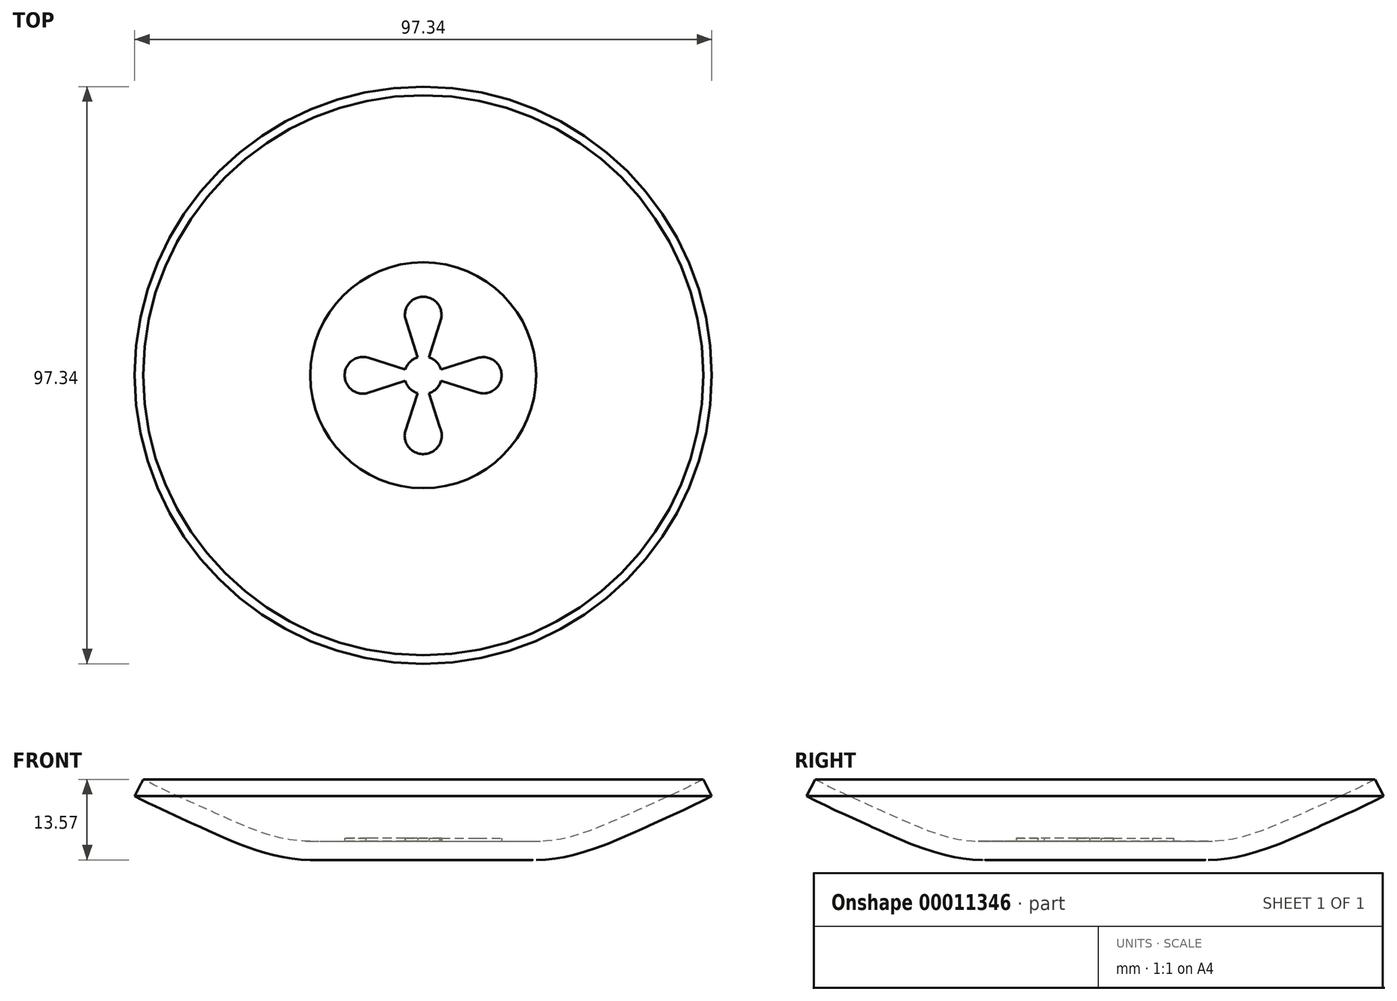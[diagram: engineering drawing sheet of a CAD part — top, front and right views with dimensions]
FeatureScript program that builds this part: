
annotation { "Feature Type Name" : "Feature", "Feature Type Description" : "" }
export const myFeature = defineFeature(function(context is Context, id is Id, definition is map)
    precondition{}
    {
        {
            var Q0;
            Q0=qCreatedBy(makeId("Front.planeOp"),FACE);
            var sketch = newSketch(context, id + "F0", { "sketchPlane" : qUnion([Q0])});
            skLineSegment(sketch, "E0", {"start": v(0, 0) * mm, "end": v(-19.05, 0) * mm});
            skFitSpline(sketch, "E1", {"points": [v(-19.05, 0) * mm, v(-36.91, 5.24) * mm, v(-48.67, 10.75) * mm], "startDerivative": vector(-35.62, 0) * mm, "endDerivative": vector(-27.78, 14.21) * mm});
            skLineSegment(sketch, "E2", {"start": v(0, 0) * mm, "end": v(0, 3.18) * mm});
            skFitSpline(sketch, "E3.0", {"points": [v(-19.05, 3.18) * mm, v(-20.31, 3.18) * mm, v(-22.88, 3.44) * mm, v(-26.8, 4.47) * mm, v(-30.02, 5.68) * mm, v(-32.52, 6.75) * mm, v(-34.34, 7.56) * mm, v(-36.1, 8.36) * mm, v(-37.78, 9.11) * mm, v(-39.37, 9.83) * mm, v(-41.44, 10.77) * mm, v(-43.96, 11.94) * mm, v(-46.1, 13) * mm, v(-47.23, 13.57) * mm]});
            skLineSegment(sketch, "E3.1", {"start": v(0, 3.18) * mm, "end": v(-19.05, 3.18) * mm});
            skLineSegment(sketch, "E4", {"start": v(-47.23, 13.57) * mm, "end": v(-48.67, 10.75) * mm});
            skSolve(sketch);
        }
        {
            var Q0;
            Q0=makeQuery(id+"F0.imprint","IMPRINT",FACE,{"disambiguationData":[TD([[makeQuery(id+"F0.imprint","IMPRINT",EDGE,{"derivedFrom":sQuery(id+"F0.wireOp",EDGE,"E0")}),-1.0]])]});
            var Q1;
            Q1=sQuery(id+"F0.wireOp",EDGE,"E2");
            revolve(context, id + "F1", {"entities" : qUnion([Q0]), "axis" : qUnion([Q1]), "revolveType" : RevolveType.FULL});
        }
        {
            var Q0;
            Q0=makeQuery(id+"F1.opRevolve","SWEPT_FACE",FACE,{"disambiguationData":[OSD([sQuery(id+"F0.wireOp",EDGE,"E3.1")])]});
            var sketch = newSketch(context, id + "F2", { "sketchPlane" : qUnion([Q0])});
            skCircle(sketch, "E5", {"center": v(0, 0) * mm, "radius": 3.18 * mm});
            skLineSegment(sketch, "E6", {"start": v(0, 0) * mm, "end": v(9.69, 3.06) * mm});
            skLineSegment(sketch, "E7", {"start": v(0, 0) * mm, "end": v(9.69, -3.06) * mm});
            skCircle(sketch, "E8", {"center": v(10.16, 0) * mm, "radius": 3.06 * mm});
            skLineSegment(sketch, "E9", {"start": v(0, 0) * mm, "end": v(3.06, 9.69) * mm});
            skLineSegment(sketch, "E10", {"start": v(0, 0) * mm, "end": v(-3.06, 9.69) * mm});
            skCircle(sketch, "E11", {"center": v(0, 10.16) * mm, "radius": 3.1 * mm});
            skLineSegment(sketch, "E12", {"start": v(0, 0) * mm, "end": v(3.06, -9.69) * mm});
            skLineSegment(sketch, "E13", {"start": v(0, 0) * mm, "end": v(-3.1, -9.68) * mm});
            skCircle(sketch, "E14", {"center": v(0, -10.16) * mm, "radius": 3.13 * mm});
            skLineSegment(sketch, "E15", {"start": v(0, 0) * mm, "end": v(-9.68, 3.1) * mm});
            skLineSegment(sketch, "E16", {"start": v(0, 0) * mm, "end": v(-9.69, -3.06) * mm});
            skCircle(sketch, "E17", {"center": v(-10.16, 0) * mm, "radius": 3.1 * mm});
            skSolve(sketch);
        }
        {
            var Q0;
            {var subQ0=sQuery(id+"F2.wireOp",EDGE,"E17");var subQ1=sQuery(id+"F2.wireOp",EDGE,"E16");var subQ4=makeQuery(id+"F2.imprint","INTERSECT",VERTEX,{"disambiguationData":[OD(0.0)],"derivedFrom":[subQ1,subQ0]});Q0=makeQuery(id+"F2.imprint","IMPRINT",FACE,{"disambiguationData":[TD([[makeQuery(id+"F2.imprint","IMPRINT",EDGE,{"disambiguationData":[TD([[subQ4,1.0]])],"derivedFrom":subQ1}),-1.0]])]});}
            var Q1;
            {var subQ3=sQuery(id+"F2.wireOp",EDGE,"E15");var subQ5=sQuery(id+"F2.wireOp",EDGE,"E5");var subQ7=makeQuery(id+"F2.imprint","INTERSECT",VERTEX,{"derivedFrom":[subQ5,subQ3]});Q1=makeQuery(id+"F2.imprint","IMPRINT",FACE,{"disambiguationData":[TD([[makeQuery(id+"F2.imprint","IMPRINT",EDGE,{"disambiguationData":[TD([[subQ7,-1.0]])],"derivedFrom":subQ5}),-1.0]])]});}
            var Q2;
            {var subQ1=sQuery(id+"F2.wireOp",EDGE,"E5");var subQ3=sQuery(id+"F2.wireOp",EDGE,"E6");var subQ5=makeQuery(id+"F2.imprint","INTERSECT",VERTEX,{"derivedFrom":[subQ1,subQ3]});Q2=makeQuery(id+"F2.imprint","IMPRINT",FACE,{"disambiguationData":[TD([[makeQuery(id+"F2.imprint","IMPRINT",EDGE,{"disambiguationData":[TD([[subQ5,1.0]])],"derivedFrom":subQ1}),1.0]])]});}
            var Q3;
            {var subQ3=sQuery(id+"F2.wireOp",EDGE,"E6");var subQ5=sQuery(id+"F2.wireOp",EDGE,"E5");var subQ7=makeQuery(id+"F2.imprint","INTERSECT",VERTEX,{"derivedFrom":[subQ5,subQ3]});Q3=makeQuery(id+"F2.imprint","IMPRINT",FACE,{"disambiguationData":[TD([[makeQuery(id+"F2.imprint","IMPRINT",EDGE,{"disambiguationData":[TD([[subQ7,1.0]])],"derivedFrom":subQ5}),-1.0]])]});}
            var Q4;
            {var subQ0=sQuery(id+"F2.wireOp",EDGE,"E8");var subQ2=makeQuery(id+"F2.imprint","INTERSECT",VERTEX,{"derivedFrom":[sQuery(id+"F2.wireOp",EDGE,"E6"),subQ0]});Q4=makeQuery(id+"F2.imprint","IMPRINT",FACE,{"disambiguationData":[TD([[makeQuery(id+"F2.imprint","IMPRINT",EDGE,{"disambiguationData":[TD([[subQ2,-1.0]])],"derivedFrom":subQ0}),1.0]])]});}
            var Q5;
            {var subQ0=sQuery(id+"F2.wireOp",EDGE,"E9");var subQ1=sQuery(id+"F2.wireOp",EDGE,"E5");var subQ2=makeQuery(id+"F2.imprint","INTERSECT",VERTEX,{"derivedFrom":[subQ1,subQ0]});Q5=makeQuery(id+"F2.imprint","IMPRINT",FACE,{"disambiguationData":[TD([[makeQuery(id+"F2.imprint","IMPRINT",EDGE,{"disambiguationData":[TD([[subQ2,1.0]])],"derivedFrom":subQ1}),1.0]])]});}
            var Q6;
            {var subQ3=sQuery(id+"F2.wireOp",EDGE,"E9");var subQ5=sQuery(id+"F2.wireOp",EDGE,"E5");var subQ7=makeQuery(id+"F2.imprint","INTERSECT",VERTEX,{"derivedFrom":[subQ5,subQ3]});Q6=makeQuery(id+"F2.imprint","IMPRINT",FACE,{"disambiguationData":[TD([[makeQuery(id+"F2.imprint","IMPRINT",EDGE,{"disambiguationData":[TD([[subQ7,-1.0]])],"derivedFrom":subQ5}),-1.0]])]});}
            var Q7;
            {var subQ0=sQuery(id+"F2.wireOp",EDGE,"E11");var subQ3=sQuery(id+"F2.wireOp",EDGE,"E9");var subQ4=makeQuery(id+"F2.imprint","INTERSECT",VERTEX,{"disambiguationData":[OD(0.0)],"derivedFrom":[subQ3,subQ0]});Q7=makeQuery(id+"F2.imprint","IMPRINT",FACE,{"disambiguationData":[TD([[makeQuery(id+"F2.imprint","IMPRINT",EDGE,{"disambiguationData":[TD([[subQ4,1.0]])],"derivedFrom":subQ3}),1.0]])]});}
            var Q8;
            {var subQ1=sQuery(id+"F2.wireOp",EDGE,"E5");var subQ3=sQuery(id+"F2.wireOp",EDGE,"E9");var subQ5=makeQuery(id+"F2.imprint","INTERSECT",VERTEX,{"derivedFrom":[subQ1,subQ3]});Q8=makeQuery(id+"F2.imprint","IMPRINT",FACE,{"disambiguationData":[TD([[makeQuery(id+"F2.imprint","IMPRINT",EDGE,{"disambiguationData":[TD([[subQ5,-1.0]])],"derivedFrom":subQ1}),1.0]])]});}
            var Q9;
            {var subQ1=sQuery(id+"F2.wireOp",EDGE,"E5");var subQ3=sQuery(id+"F2.wireOp",EDGE,"E10");var subQ5=makeQuery(id+"F2.imprint","INTERSECT",VERTEX,{"derivedFrom":[subQ1,subQ3]});Q9=makeQuery(id+"F2.imprint","IMPRINT",FACE,{"disambiguationData":[TD([[makeQuery(id+"F2.imprint","IMPRINT",EDGE,{"disambiguationData":[TD([[subQ5,-1.0]])],"derivedFrom":subQ1}),1.0]])]});}
            var Q10;
            {var subQ1=sQuery(id+"F2.wireOp",EDGE,"E5");var subQ3=sQuery(id+"F2.wireOp",EDGE,"E15");var subQ5=makeQuery(id+"F2.imprint","INTERSECT",VERTEX,{"derivedFrom":[subQ1,subQ3]});Q10=makeQuery(id+"F2.imprint","IMPRINT",FACE,{"disambiguationData":[TD([[makeQuery(id+"F2.imprint","IMPRINT",EDGE,{"disambiguationData":[TD([[subQ5,-1.0]])],"derivedFrom":subQ1}),1.0]])]});}
            var Q11;
            {var subQ0=sQuery(id+"F2.wireOp",EDGE,"E16");var subQ1=sQuery(id+"F2.wireOp",EDGE,"E5");var subQ2=makeQuery(id+"F2.imprint","INTERSECT",VERTEX,{"derivedFrom":[subQ1,subQ0]});Q11=makeQuery(id+"F2.imprint","IMPRINT",FACE,{"disambiguationData":[TD([[makeQuery(id+"F2.imprint","IMPRINT",EDGE,{"disambiguationData":[TD([[subQ2,-1.0]])],"derivedFrom":subQ1}),1.0]])]});}
            var Q12;
            {var subQ0=sQuery(id+"F2.wireOp",EDGE,"E12");var subQ1=sQuery(id+"F2.wireOp",EDGE,"E5");var subQ2=makeQuery(id+"F2.imprint","INTERSECT",VERTEX,{"derivedFrom":[subQ1,subQ0]});Q12=makeQuery(id+"F2.imprint","IMPRINT",FACE,{"disambiguationData":[TD([[makeQuery(id+"F2.imprint","IMPRINT",EDGE,{"disambiguationData":[TD([[subQ2,-1.0]])],"derivedFrom":subQ1}),1.0]])]});}
            var Q13;
            {var subQ0=sQuery(id+"F2.wireOp",EDGE,"E13");var subQ1=sQuery(id+"F2.wireOp",EDGE,"E5");var subQ2=makeQuery(id+"F2.imprint","INTERSECT",VERTEX,{"derivedFrom":[subQ1,subQ0]});Q13=makeQuery(id+"F2.imprint","IMPRINT",FACE,{"disambiguationData":[TD([[makeQuery(id+"F2.imprint","IMPRINT",EDGE,{"disambiguationData":[TD([[subQ2,-1.0]])],"derivedFrom":subQ1}),1.0]])]});}
            var Q14;
            {var subQ0=sQuery(id+"F2.wireOp",EDGE,"E13");var subQ3=sQuery(id+"F2.wireOp",EDGE,"E5");var subQ4=makeQuery(id+"F2.imprint","INTERSECT",VERTEX,{"derivedFrom":[subQ3,subQ0]});Q14=makeQuery(id+"F2.imprint","IMPRINT",FACE,{"disambiguationData":[TD([[makeQuery(id+"F2.imprint","IMPRINT",EDGE,{"disambiguationData":[TD([[subQ4,-1.0]])],"derivedFrom":subQ3}),-1.0]])]});}
            var Q15;
            {var subQ0=sQuery(id+"F2.wireOp",EDGE,"E14");var subQ2=sQuery(id+"F2.wireOp",EDGE,"E13");var subQ3=makeQuery(id+"F2.imprint","INTERSECT",VERTEX,{"disambiguationData":[OD(0.0)],"derivedFrom":[subQ2,subQ0]});Q15=makeQuery(id+"F2.imprint","IMPRINT",FACE,{"disambiguationData":[TD([[makeQuery(id+"F2.imprint","IMPRINT",EDGE,{"disambiguationData":[TD([[subQ3,1.0]])],"derivedFrom":subQ2}),1.0]])]});}
            extrude(context, id + "F3", {"entities" : qUnion([Q0, Q1, Q2, Q3, Q4, Q5, Q6, Q7, Q8, Q9, Q10, Q11, Q12, Q13, Q14, Q15]), "operationType" : NewBodyOperationType.ADD, "depth" : 0.5 * mm});
        }
    });
